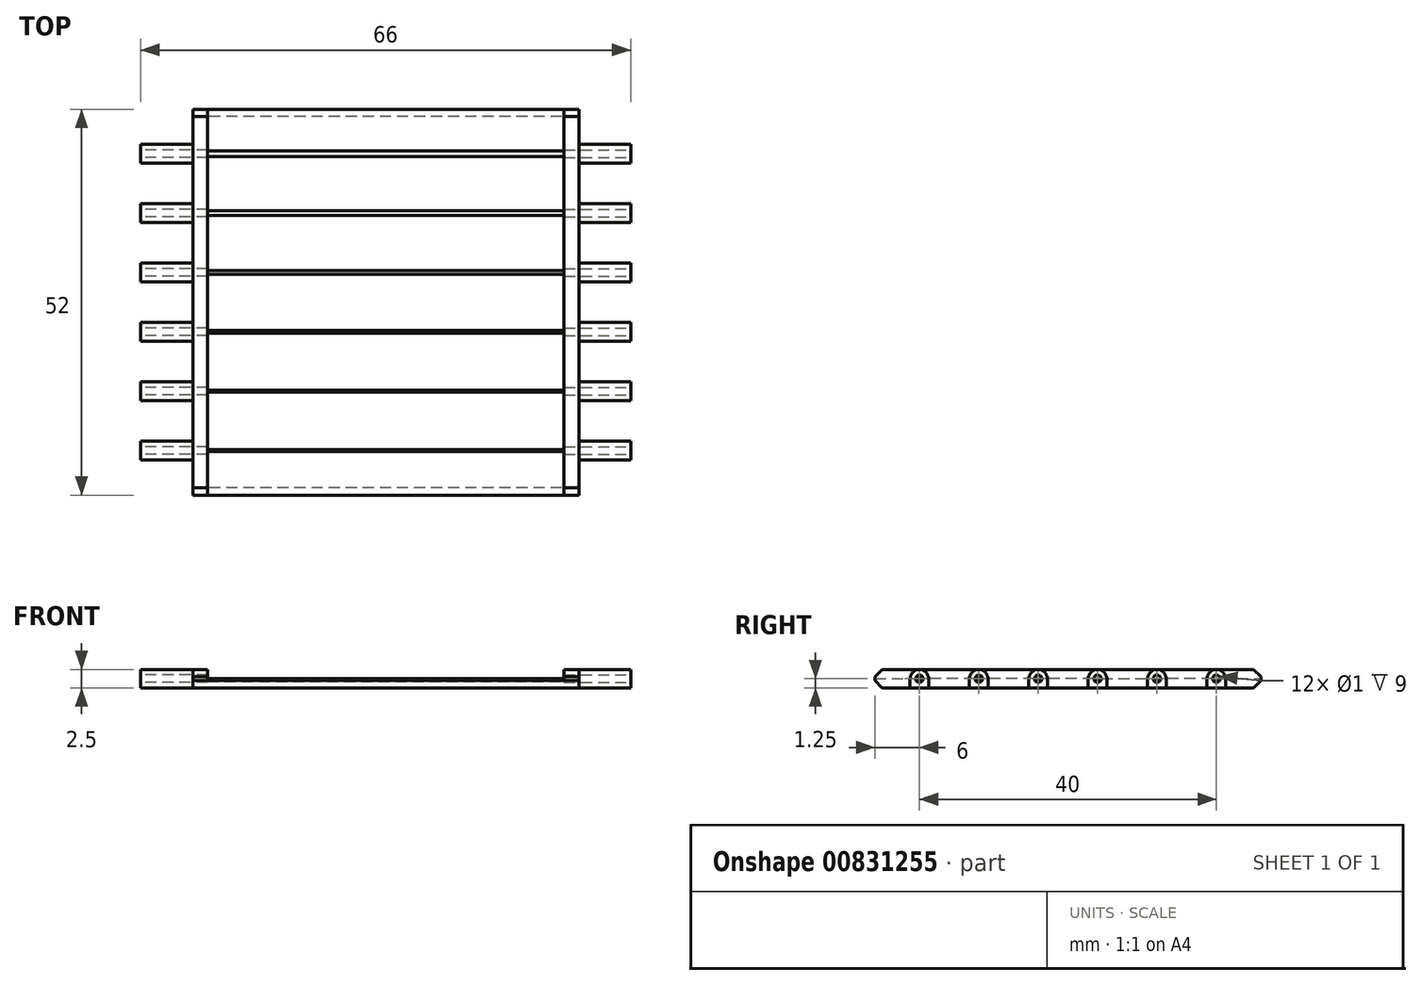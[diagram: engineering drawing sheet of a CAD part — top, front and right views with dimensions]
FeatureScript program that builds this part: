
annotation { "Feature Type Name" : "Feature", "Feature Type Description" : "" }
export const myFeature = defineFeature(function(context is Context, id is Id, definition is map)
    precondition{}
    {
        {
            var Q0;
            Q0=qCreatedBy(makeId("Top.planeOp"),FACE);
            var sketch = newSketch(context, id + "F0", { "sketchPlane" : qUnion([Q0])});
            skLineSegment(sketch, "E0", {"start": v(0, 0) * mm, "end": v(0, 52) * mm});
            skLineSegment(sketch, "E1", {"start": v(0, 52) * mm, "end": v(70, 52) * mm});
            skLineSegment(sketch, "E2", {"start": v(70, 52) * mm, "end": v(70, 0) * mm});
            skLineSegment(sketch, "E3", {"start": v(70, 0) * mm, "end": v(0, 0) * mm});
            skSolve(sketch);
        }
        {
            var Q0;
            Q0=makeQuery(id+"F0.imprint","IMPRINT",FACE,{"disambiguationData":[TD([[makeQuery(id+"F0.imprint","IMPRINT",EDGE,{"derivedFrom":sQuery(id+"F0.wireOp",EDGE,"E0")}),-1.0]])]});
            extrude(context, id + "F1", {"entities" : qUnion([Q0]), "depth" : 2.5 * mm, "offsetDistance" : 25 * mm});
        }
        {
            var Q0;
            Q0=makeQuery(id+"F1.opExtrude","SWEPT_FACE",FACE,{"disambiguationData":[OSD([sQuery(id+"F0.wireOp",EDGE,"E0")])]});
            var sketch = newSketch(context, id + "F2", { "sketchPlane" : qUnion([Q0])});
            skLineSegment(sketch, "E4", {"start": v(-52, 1.25) * mm, "end": v(-46, 1.25) * mm, "construction": true});
            skLineSegment(sketch, "E5", {"start": v(-46, 1.25) * mm, "end": v(-38, 1.25) * mm, "construction": true});
            skLineSegment(sketch, "E6", {"start": v(-38, 1.25) * mm, "end": v(-30, 1.25) * mm, "construction": true});
            skLineSegment(sketch, "E7", {"start": v(-30, 1.25) * mm, "end": v(-22, 1.25) * mm, "construction": true});
            skLineSegment(sketch, "E8", {"start": v(-22, 1.25) * mm, "end": v(-14, 1.25) * mm, "construction": true});
            skLineSegment(sketch, "E9", {"start": v(-14, 1.25) * mm, "end": v(-6, 1.25) * mm, "construction": true});
            skLineSegment(sketch, "E10", {"start": v(-6, 1.25) * mm, "end": v(0, 1.25) * mm, "construction": true});
            skCircle(sketch, "E11", {"center": v(-46, 1.25) * mm, "radius": 0.5 * mm});
            skCircle(sketch, "E12", {"center": v(-38, 1.25) * mm, "radius": 0.5 * mm});
            skCircle(sketch, "E13", {"center": v(-30, 1.25) * mm, "radius": 0.5 * mm});
            skCircle(sketch, "E14", {"center": v(-22, 1.25) * mm, "radius": 0.5 * mm});
            skCircle(sketch, "E15", {"center": v(-14, 1.25) * mm, "radius": 0.5 * mm});
            skCircle(sketch, "E16", {"center": v(-6, 1.25) * mm, "radius": 0.5 * mm});
            skLineSegment(sketch, "E17", {"start": v(-6, 0) * mm, "end": v(-6, 1.25) * mm, "construction": true});
            skSolve(sketch);
        }
        {
            var Q0;
            Q0 = qSketchRegion(id + "F2", true);
            extrude(context, id + "F3", {"entities" : qUnion([Q0]), "operationType" : NewBodyOperationType.REMOVE, "oppositeDirection" : true, "depth" : 2 * mm, "offsetDistance" : 25 * mm});
        }
        {
            var Q0;
            Q0=makeQuery(id+"F1.opExtrude","SWEPT_FACE",FACE,{"disambiguationData":[OSD([sQuery(id+"F0.wireOp",EDGE,"E0")])]});
            var sketch = newSketch(context, id + "F4", { "sketchPlane" : qUnion([Q0])});
            skLineSegment(sketch, "E18", {"start": v(-44.75, 1.25) * mm, "end": v(-44.75, 0) * mm});
            skLineSegment(sketch, "E19", {"start": v(-47.25, 1.25) * mm, "end": v(-47.25, 0) * mm});
            skLineSegment(sketch, "E20", {"start": v(-47.25, 0) * mm, "end": v(-44.75, 0) * mm});
            skArc(sketch, "E21", {"start": v(-47.25, 1.25) * mm, "mid": v(-46, 2.5) * mm, "end": v(-44.75, 1.25) * mm});
            skLineSegment(sketch, "E22", {"start": v(-36.75, 1.25) * mm, "end": v(-36.75, 0) * mm});
            skLineSegment(sketch, "E23", {"start": v(-39.25, 1.25) * mm, "end": v(-39.25, 0) * mm});
            skLineSegment(sketch, "E24", {"start": v(-39.25, 0) * mm, "end": v(-36.75, 0) * mm});
            skArc(sketch, "E25", {"start": v(-39.25, 1.25) * mm, "mid": v(-38, 2.5) * mm, "end": v(-36.75, 1.25) * mm});
            skLineSegment(sketch, "E26", {"start": v(-28.75, 1.25) * mm, "end": v(-28.75, 0) * mm});
            skLineSegment(sketch, "E27", {"start": v(-31.25, 1.25) * mm, "end": v(-31.25, 0) * mm});
            skLineSegment(sketch, "E28", {"start": v(-31.25, 0) * mm, "end": v(-28.75, 0) * mm});
            skArc(sketch, "E29", {"start": v(-31.25, 1.25) * mm, "mid": v(-30, 2.5) * mm, "end": v(-28.75, 1.25) * mm});
            skLineSegment(sketch, "E30", {"start": v(-20.75, 1.25) * mm, "end": v(-20.75, 0) * mm});
            skLineSegment(sketch, "E31", {"start": v(-23.25, 1.25) * mm, "end": v(-23.25, 0) * mm});
            skLineSegment(sketch, "E32", {"start": v(-23.25, 0) * mm, "end": v(-20.75, 0) * mm});
            skArc(sketch, "E33", {"start": v(-23.25, 1.25) * mm, "mid": v(-22, 2.5) * mm, "end": v(-20.75, 1.25) * mm});
            skLineSegment(sketch, "E34", {"start": v(-12.75, 1.25) * mm, "end": v(-12.75, 0) * mm});
            skLineSegment(sketch, "E35", {"start": v(-15.25, 1.25) * mm, "end": v(-15.25, 0) * mm});
            skLineSegment(sketch, "E36", {"start": v(-15.25, 0) * mm, "end": v(-12.75, 0) * mm});
            skArc(sketch, "E37", {"start": v(-15.25, 1.25) * mm, "mid": v(-14, 2.5) * mm, "end": v(-12.75, 1.25) * mm});
            skLineSegment(sketch, "E38", {"start": v(-4.75, 1.25) * mm, "end": v(-4.75, 0) * mm});
            skLineSegment(sketch, "E39", {"start": v(-7.25, 1.25) * mm, "end": v(-7.25, 0) * mm});
            skLineSegment(sketch, "E40", {"start": v(-7.25, 0) * mm, "end": v(-4.75, 0) * mm});
            skArc(sketch, "E41", {"start": v(-7.25, 1.25) * mm, "mid": v(-6, 2.5) * mm, "end": v(-4.75, 1.25) * mm});
            skSolve(sketch);
        }
        {
            var Q0;
            Q0 = qSketchRegion(id + "F4", true);
            extrude(context, id + "F5", {"entities" : qUnion([Q0]), "operationType" : NewBodyOperationType.ADD, "depth" : 7 * mm, "offsetDistance" : 25 * mm});
        }
        {
            var Q0;
            Q0=makeQuery(id+"F1.opExtrude","CAP_FACE",FACE,{"disambiguationData":[OSD([sQuery(id+"F0.wireOp",EDGE,"E0"),sQuery(id+"F0.wireOp",EDGE,"E1"),sQuery(id+"F0.wireOp",EDGE,"E2"),sQuery(id+"F0.wireOp",EDGE,"E3")])],"isStart":false});
            var sketch = newSketch(context, id + "F6", { "sketchPlane" : qUnion([Q0])});
            skPoint(sketch, "E42.0", {"position": v(70, 0) * mm});
            skPoint(sketch, "E42.1", {"position": v(70, 52) * mm});
            skLineSegment(sketch, "E43", {"start": v(70, 52) * mm, "end": v(70, 0) * mm});
            skLineSegment(sketch, "E44", {"start": v(70, 0) * mm, "end": v(26, 0) * mm});
            skLineSegment(sketch, "E45", {"start": v(70, 52) * mm, "end": v(26, 52) * mm});
            skLineSegment(sketch, "E46", {"start": v(26, 52) * mm, "end": v(26, 0) * mm});
            skSolve(sketch);
        }
        {
            var Q0;
            Q0 = qSketchRegion(id + "F6", true);
            extrude(context, id + "F7", {"entities" : qUnion([Q0]), "operationType" : NewBodyOperationType.REMOVE, "oppositeDirection" : true, "depth" : 25 * mm, "offsetDistance" : 25 * mm});
        }
        {
            var Q0;
            Q0=makeQuery(id+"F7.boolean.opBoolean","COPY",FACE,{"derivedFrom":makeQuery(id+"F7.opExtrude","SWEPT_FACE",FACE,{"disambiguationData":[OSD([sQuery(id+"F6.wireOp",EDGE,"E46")])]})});
            cPlane(context, id + "F8", {"entities" : qUnion([Q0]), "cplaneType" : CPlaneType.OFFSET, "offset" : 0 * mm, "width" : 150 * mm, "height" : 150 * mm});
        }
        {
            var Q0;
            Q0=makeQuery(id+"F1.opExtrude","SWEPT_BODY",BODY,{"disambiguationData":[OSD([sQuery(id+"F0.wireOp",EDGE,"E0"),sQuery(id+"F0.wireOp",EDGE,"E1"),sQuery(id+"F0.wireOp",EDGE,"E2"),sQuery(id+"F0.wireOp",EDGE,"E3")])]});
            var Q1;
            Q1=qCreatedBy(id+"F8.planeOp",FACE);
            mirror(context, id + "F9", {"operationType" : NewBodyOperationType.ADD, "entities" : qUnion([Q0]), "mirrorPlane" : qUnion([Q1])});
        }
        {
            var Q0;
            {var subQ0=makeQuery(id+"F1.opExtrude","CAP_FACE",FACE,{"disambiguationData":[OSD([sQuery(id+"F0.wireOp",EDGE,"E0"),sQuery(id+"F0.wireOp",EDGE,"E1"),sQuery(id+"F0.wireOp",EDGE,"E2"),sQuery(id+"F0.wireOp",EDGE,"E3")])],"isStart":false});Q0=makeQuery(id+"F9.boolean.opBoolean","MERGE",FACE,{"derivedFrom":[subQ0,makeQuery(id+"F9.opPattern","COPY",FACE,{"derivedFrom":subQ0,"instanceName":"1"})]});}
            var sketch = newSketch(context, id + "F10", { "sketchPlane" : qUnion([Q0])});
            skLineSegment(sketch, "E47", {"start": v(2, 52) * mm, "end": v(50, 52) * mm});
            skLineSegment(sketch, "E48", {"start": v(50, 52) * mm, "end": v(50, 0) * mm});
            skLineSegment(sketch, "E49", {"start": v(50, 0) * mm, "end": v(2, 0) * mm});
            skLineSegment(sketch, "E50", {"start": v(2, 0) * mm, "end": v(2, 52) * mm});
            skSolve(sketch);
        }
        {
            var Q0;
            Q0 = qSketchRegion(id + "F10", true);
            var Q1;
            Q1 = qSketchRegion(id + "F12", true);
            extrude(context, id + "F11", {"entities" : qUnion([Q0, Q1]), "operationType" : NewBodyOperationType.REMOVE, "oppositeDirection" : true, "depth" : 1.25 * mm, "offsetDistance" : 25 * mm});
        }
        {
            var Q0;
            Q0=makeQuery(id+"F11.boolean.opBoolean","COPY",FACE,{"derivedFrom":makeQuery(id+"F11.opExtrude","CAP_FACE",FACE,{"disambiguationData":[OSD([sQuery(id+"F10.wireOp",EDGE,"E47"),sQuery(id+"F10.wireOp",EDGE,"E48"),sQuery(id+"F10.wireOp",EDGE,"E49"),sQuery(id+"F10.wireOp",EDGE,"E50")])],"isStart":false})});
            var sketch = newSketch(context, id + "F12", { "sketchPlane" : qUnion([Q0])});
            skLineSegment(sketch, "E51", {"start": v(2, 5.9) * mm, "end": v(2, 6.1) * mm});
            skLineSegment(sketch, "E52.0", {"start": v(50, 46.38) * mm, "end": v(50, 45.63) * mm});
            skLineSegment(sketch, "E52.4", {"start": v(50, 14.38) * mm, "end": v(50, 13.63) * mm, "construction": true});
            skLineSegment(sketch, "E53", {"start": v(2, 5.9) * mm, "end": v(50, 5.9) * mm});
            skLineSegment(sketch, "E54", {"start": v(2, 6.1) * mm, "end": v(50, 6.1) * mm});
            skLineSegment(sketch, "E55", {"start": v(50, 5.9) * mm, "end": v(50, 6.1) * mm});
            skLineSegment(sketch, "E56", {"start": v(2, 5.63) * mm, "end": v(2, 6.38) * mm, "construction": true});
            skLineSegment(sketch, "E57", {"start": v(2, 14) * mm, "end": v(2, 14.15) * mm});
            skLineSegment(sketch, "E58", {"start": v(2, 14) * mm, "end": v(2, 13.85) * mm});
            skLineSegment(sketch, "E59", {"start": v(2, 13.85) * mm, "end": v(50, 13.85) * mm});
            skLineSegment(sketch, "E60", {"start": v(2, 14.15) * mm, "end": v(50, 14.15) * mm});
            skLineSegment(sketch, "E61", {"start": v(50, 13.85) * mm, "end": v(50, 14.15) * mm});
            skLineSegment(sketch, "E62", {"start": v(2, 22) * mm, "end": v(2, 22.2) * mm});
            skLineSegment(sketch, "E63", {"start": v(2, 22) * mm, "end": v(2, 21.8) * mm});
            skLineSegment(sketch, "E64", {"start": v(2, 21.8) * mm, "end": v(50, 21.8) * mm});
            skLineSegment(sketch, "E65", {"start": v(50, 21.8) * mm, "end": v(50, 22.2) * mm});
            skLineSegment(sketch, "E66", {"start": v(50, 22.2) * mm, "end": v(2, 22.2) * mm});
            skLineSegment(sketch, "E67", {"start": v(2, 30) * mm, "end": v(2, 30.25) * mm});
            skLineSegment(sketch, "E68", {"start": v(2, 30) * mm, "end": v(2, 29.75) * mm});
            skLineSegment(sketch, "E69", {"start": v(2, 29.75) * mm, "end": v(50, 29.75) * mm});
            skLineSegment(sketch, "E70", {"start": v(50, 29.75) * mm, "end": v(50, 30.25) * mm});
            skLineSegment(sketch, "E71", {"start": v(50, 30.25) * mm, "end": v(2, 30.25) * mm});
            skLineSegment(sketch, "E72", {"start": v(2, 38) * mm, "end": v(2, 38.3) * mm});
            skLineSegment(sketch, "E73", {"start": v(2, 38) * mm, "end": v(2, 37.7) * mm});
            skLineSegment(sketch, "E74", {"start": v(2, 37.7) * mm, "end": v(50, 37.7) * mm});
            skLineSegment(sketch, "E75", {"start": v(50, 37.7) * mm, "end": v(50, 38.3) * mm});
            skLineSegment(sketch, "E76", {"start": v(50, 38.3) * mm, "end": v(2, 38.3) * mm});
            skLineSegment(sketch, "E77.0", {"start": v(2, 45.63) * mm, "end": v(2, 46.38) * mm});
            skLineSegment(sketch, "E78", {"start": v(2, 45.63) * mm, "end": v(50, 45.63) * mm});
            skLineSegment(sketch, "E79", {"start": v(50, 46.38) * mm, "end": v(2, 46.38) * mm});
            skSolve(sketch);
        }
        {
            var Q0;
            Q0 = qSketchRegion(id + "F12", true);
            extrude(context, id + "F13", {"entities" : qUnion([Q0]), "operationType" : NewBodyOperationType.REMOVE, "oppositeDirection" : true, "depth" : 0.38 * mm, "offsetDistance" : 25 * mm});
        }
        {
            var Q0;
            {var subQ0=sQuery(id+"F0.wireOp",EDGE,"E1");var subQ1=sQuery(id+"F0.wireOp",EDGE,"E3");var subQ2=sQuery(id+"F0.wireOp",EDGE,"E2");var subQ3=sQuery(id+"F0.wireOp",EDGE,"E0");var subQ4=makeQuery(id+"F1.opExtrude","SWEPT_FACE",FACE,{"disambiguationData":[OSD([subQ3])]});Q0=makeQuery(id+"F5.boolean.opBoolean","SPLIT",FACE,{"disambiguationData":[TD([subQ4,makeQuery(id+"F1.opExtrude","CAP_FACE",FACE,{"disambiguationData":[OSD([subQ3,subQ0,subQ2,subQ1])],"isStart":true}),makeQuery(id+"F1.opExtrude","CAP_FACE",FACE,{"disambiguationData":[OSD([subQ3,subQ0,subQ2,subQ1])],"isStart":false}),makeQuery(id+"F1.opExtrude","SWEPT_FACE",FACE,{"disambiguationData":[OSD([subQ0])]}),makeQuery(id+"F5.opExtrude","SWEPT_FACE",FACE,{"disambiguationData":[OSD([sQuery(id+"F4.wireOp",EDGE,"f156c34e-923b-40a0-8372-4391a889fc8d")])]})])],"derivedFrom":subQ4});}
            var sketch = newSketch(context, id + "F14", { "sketchPlane" : qUnion([Q0])});
            skLineSegment(sketch, "E80", {"start": v(-52, 2.5) * mm, "end": v(-51, 2.5) * mm});
            skLineSegment(sketch, "E81", {"start": v(-52, 2.5) * mm, "end": v(-52, 1.5) * mm});
            skLineSegment(sketch, "E82", {"start": v(-52, 0) * mm, "end": v(-52, 1) * mm});
            skLineSegment(sketch, "E83", {"start": v(-52, 0) * mm, "end": v(-51, 0) * mm});
            skLineSegment(sketch, "E84", {"start": v(-52, 1.5) * mm, "end": v(-51, 2.5) * mm});
            skLineSegment(sketch, "E85", {"start": v(-52, 1) * mm, "end": v(-51, 0) * mm});
            skLineSegment(sketch, "E86", {"start": v(0, 0) * mm, "end": v(0, 1) * mm});
            skLineSegment(sketch, "E87", {"start": v(0, 0) * mm, "end": v(-1, 0) * mm});
            skPoint(sketch, "E88.0", {"position": v(0, 2.5) * mm});
            skLineSegment(sketch, "E89", {"start": v(0, 2.5) * mm, "end": v(-1, 2.5) * mm});
            skLineSegment(sketch, "E90", {"start": v(0, 2.5) * mm, "end": v(0, 1.5) * mm});
            skLineSegment(sketch, "E91", {"start": v(-1, 2.5) * mm, "end": v(0, 1.5) * mm});
            skLineSegment(sketch, "E92", {"start": v(-1, 0) * mm, "end": v(0, 1) * mm});
            skSolve(sketch);
        }
        {
            var Q0;
            Q0 = qSketchRegion(id + "F14", true);
            extrude(context, id + "F15", {"entities" : qUnion([Q0]), "operationType" : NewBodyOperationType.REMOVE, "oppositeDirection" : true, "depth" : 60 * mm, "offsetDistance" : 25 * mm});
        }
        {
            var Q0;
            Q0=makeQuery(id+"F5.opExtrude","CAP_FACE",FACE,{"disambiguationData":[OSD([sQuery(id+"F4.wireOp",EDGE,"E18"),sQuery(id+"F4.wireOp",EDGE,"E19"),sQuery(id+"F4.wireOp",EDGE,"E20"),sQuery(id+"F4.wireOp",EDGE,"E21")])],"isStart":false});
            var sketch = newSketch(context, id + "F16", { "sketchPlane" : qUnion([Q0])});
            skCircle(sketch, "E93", {"center": v(-46, 1.25) * mm, "radius": 0.5 * mm});
            skCircle(sketch, "E94", {"center": v(-38, 1.25) * mm, "radius": 0.5 * mm});
            skCircle(sketch, "E95", {"center": v(-30, 1.25) * mm, "radius": 0.5 * mm});
            skCircle(sketch, "E96", {"center": v(-22, 1.25) * mm, "radius": 0.5 * mm});
            skCircle(sketch, "E97", {"center": v(-14, 1.25) * mm, "radius": 0.5 * mm});
            skCircle(sketch, "E98", {"center": v(-6, 1.25) * mm, "radius": 0.5 * mm});
            skSolve(sketch);
        }
        {
            var Q0;
            Q0 = qSketchRegion(id + "F16", true);
            extrude(context, id + "F17", {"entities" : qUnion([Q0]), "operationType" : NewBodyOperationType.REMOVE, "oppositeDirection" : true, "depth" : 9 * mm, "offsetDistance" : 25 * mm});
        }
        {
            var Q0;
            Q0=makeQuery(id+"F9.opPattern","COPY",FACE,{"derivedFrom":makeQuery(id+"F5.opExtrude","CAP_FACE",FACE,{"disambiguationData":[OSD([sQuery(id+"F4.wireOp",EDGE,"E38"),sQuery(id+"F4.wireOp",EDGE,"E39"),sQuery(id+"F4.wireOp",EDGE,"E40"),sQuery(id+"F4.wireOp",EDGE,"E41")])],"isStart":false}),"instanceName":"1"});
            var sketch = newSketch(context, id + "F18", { "sketchPlane" : qUnion([Q0])});
            skCircle(sketch, "E99", {"center": v(6, 1.25) * mm, "radius": 0.5 * mm});
            skCircle(sketch, "E100", {"center": v(14, 1.25) * mm, "radius": 0.5 * mm});
            skCircle(sketch, "E101", {"center": v(22, 1.25) * mm, "radius": 0.5 * mm});
            skCircle(sketch, "E102", {"center": v(30, 1.25) * mm, "radius": 0.5 * mm});
            skCircle(sketch, "E103", {"center": v(38, 1.25) * mm, "radius": 0.5 * mm});
            skCircle(sketch, "E104", {"center": v(46, 1.25) * mm, "radius": 0.5 * mm});
            skSolve(sketch);
        }
        {
            var Q0;
            Q0 = qSketchRegion(id + "F18", true);
            extrude(context, id + "F19", {"entities" : qUnion([Q0]), "operationType" : NewBodyOperationType.REMOVE, "oppositeDirection" : true, "depth" : 9 * mm, "offsetDistance" : 25 * mm});
        }
    });
